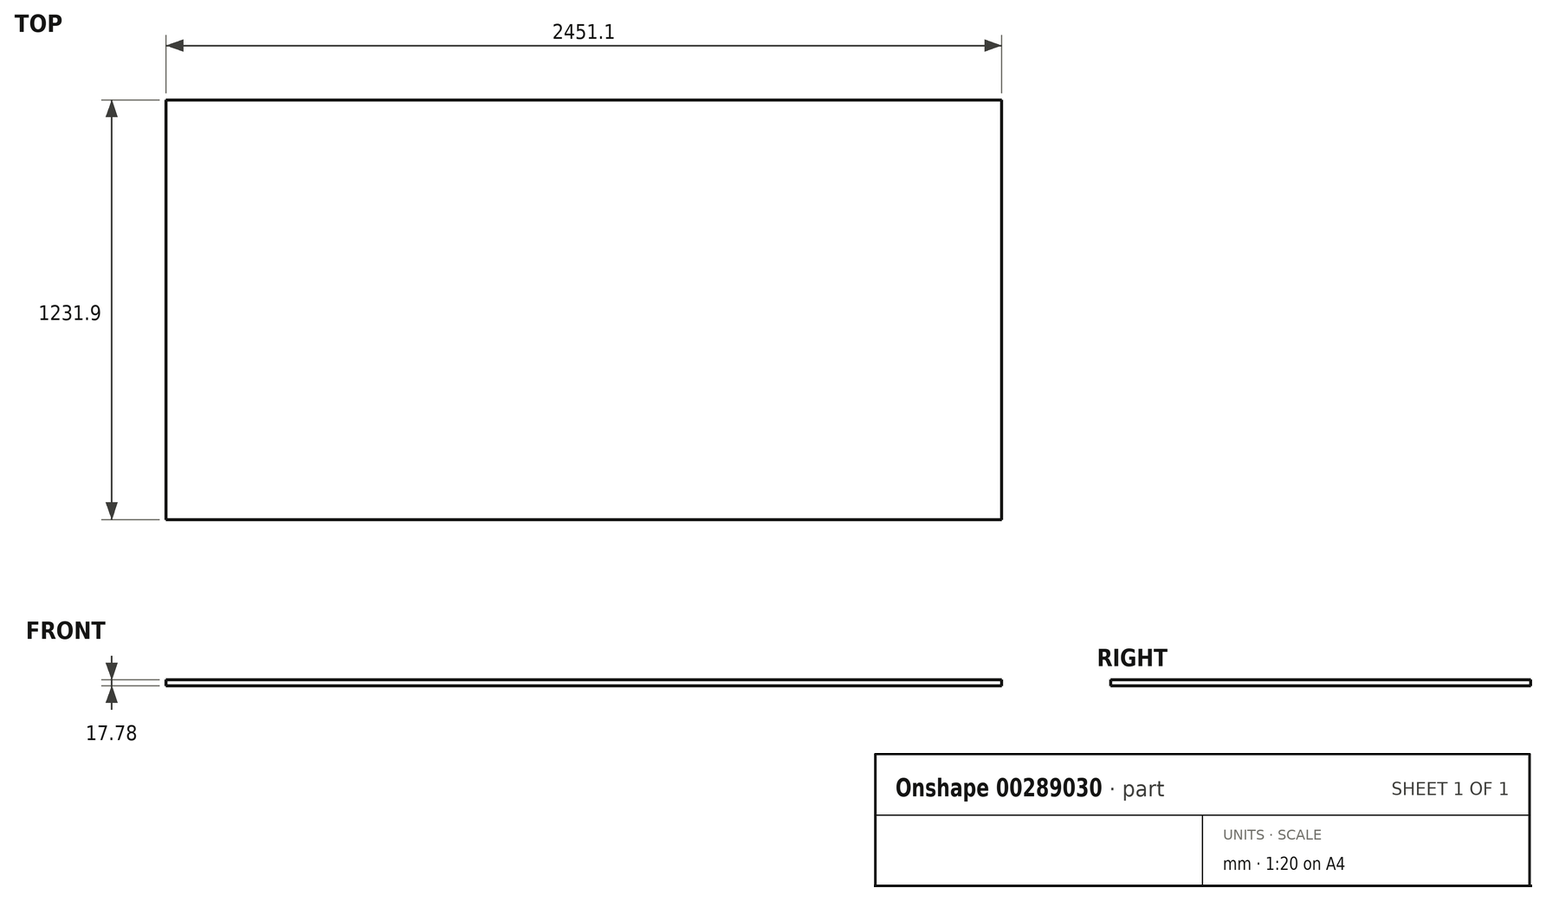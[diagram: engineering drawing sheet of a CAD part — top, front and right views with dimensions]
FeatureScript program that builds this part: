
annotation { "Feature Type Name" : "Feature", "Feature Type Description" : "" }
export const myFeature = defineFeature(function(context is Context, id is Id, definition is map)
    precondition{}
    {
        {
            var Q0;
            Q0=qCreatedBy(makeId("Top.planeOp"),FACE);
            var sketch = newSketch(context, id + "F0", { "sketchPlane" : qUnion([Q0])});
            skLineSegment(sketch, "E0.bottom", {"start": v(-1225.55, -615.95) * mm, "end": v(1225.55, -615.95) * mm});
            skLineSegment(sketch, "E0.top", {"start": v(-1225.55, 615.95) * mm, "end": v(1225.55, 615.95) * mm});
            skLineSegment(sketch, "E0.left", {"start": v(-1225.55, -615.95) * mm, "end": v(-1225.55, 615.95) * mm});
            skLineSegment(sketch, "E0.right", {"start": v(1225.55, -615.95) * mm, "end": v(1225.55, 615.95) * mm});
            skPoint(sketch, "E0.middle", {"position": v(0, 0) * mm});
            skSolve(sketch);
        }
        {
            var Q0;
            Q0=makeQuery(id+"F0.imprint","IMPRINT",FACE,{"disambiguationData":[TD([[makeQuery(id+"F0.imprint","IMPRINT",EDGE,{"derivedFrom":sQuery(id+"F0.wireOp",EDGE,"E0.bottom")}),1.0]])]});
            extrude(context, id + "F1", {"entities" : qUnion([Q0]), "depth" : 17.78 * mm});
        }
    });
